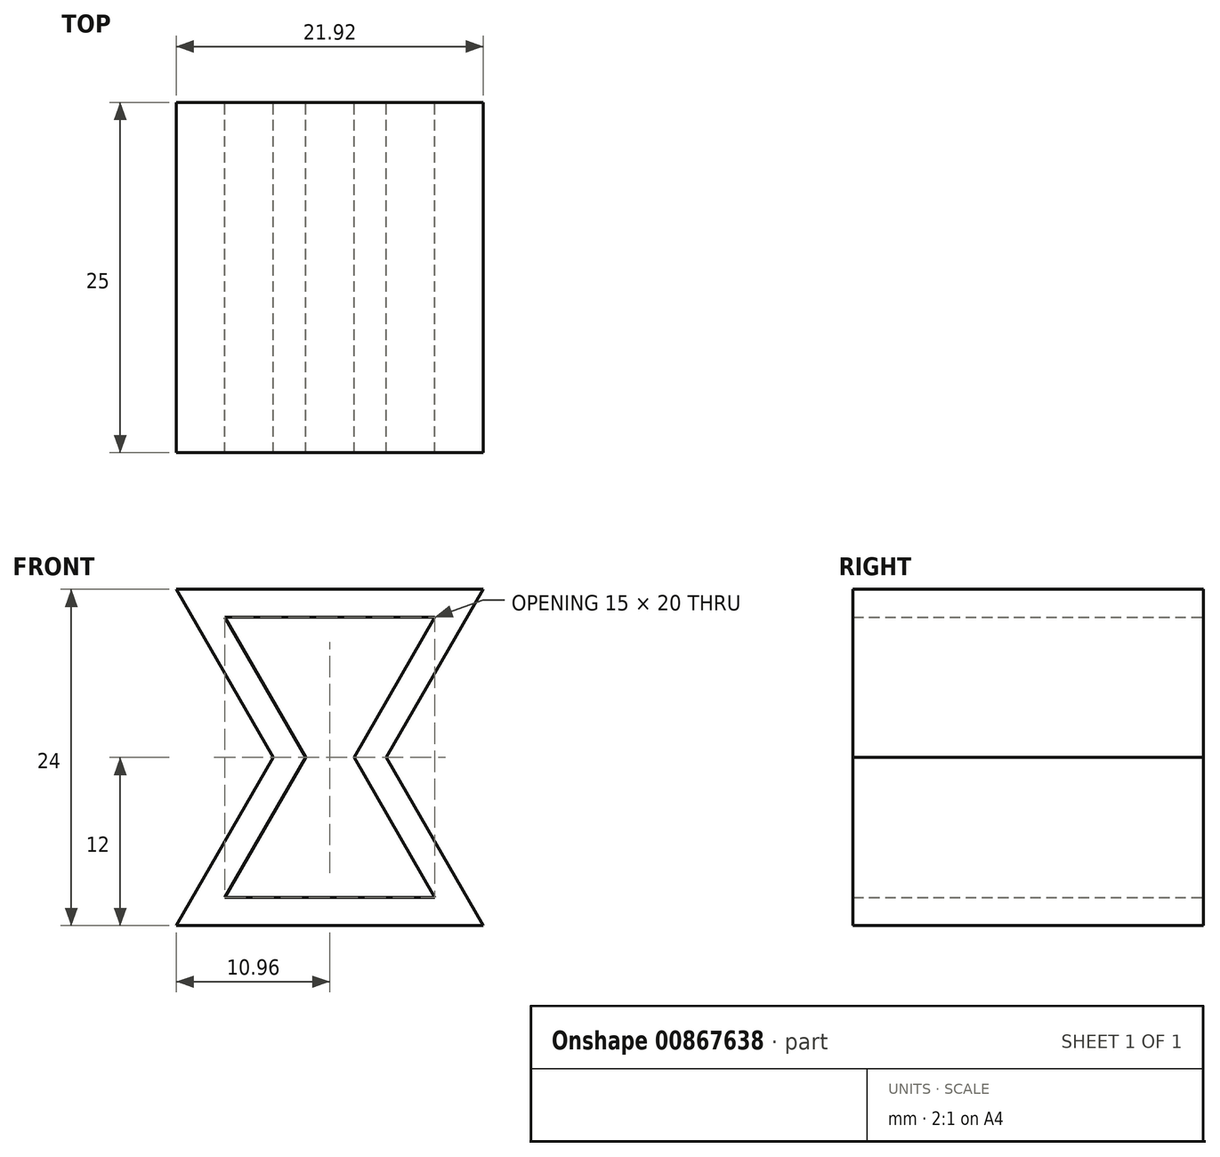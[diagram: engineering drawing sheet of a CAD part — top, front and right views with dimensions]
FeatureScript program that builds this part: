
annotation { "Feature Type Name" : "Feature", "Feature Type Description" : "" }
export const myFeature = defineFeature(function(context is Context, id is Id, definition is map)
    precondition{}
    {
        {
            var Q0;
            Q0=qCreatedBy(makeId("Front.planeOp"),FACE);
            var sketch = newSketch(context, id + "F0", { "sketchPlane" : qUnion([Q0])});
            skLineSegment(sketch, "E0", {"start": v(0, 0) * mm, "end": v(15, 0) * mm});
            skLineSegment(sketch, "E1", {"start": v(0, 20) * mm, "end": v(15, 20) * mm});
            skLineSegment(sketch, "E2", {"start": v(0, 20) * mm, "end": v(5.77, 10) * mm});
            skLineSegment(sketch, "E3", {"start": v(5.77, 10) * mm, "end": v(0, 0) * mm});
            skLineSegment(sketch, "E4", {"start": v(15, 20) * mm, "end": v(9.23, 10) * mm});
            skLineSegment(sketch, "E5", {"start": v(9.23, 10) * mm, "end": v(15, 0) * mm});
            skPoint(sketch, "E6", {"position": v(7.5, 22) * mm});
            skPoint(sketch, "E6.positionSnap0", {"position": v(7.5, 20) * mm});
            skPoint(sketch, "E7", {"position": v(7.5, -2) * mm});
            skPoint(sketch, "E7.positionSnap0", {"position": v(7.5, 0) * mm});
            skPoint(sketch, "E8", {"position": v(0.57, 5) * mm});
            skLineSegment(sketch, "E9", {"start": v(0.57, 5) * mm, "end": v(-3.46, -2) * mm});
            skPoint(sketch, "E10", {"position": v(14.43, 5) * mm});
            skLineSegment(sketch, "E11", {"start": v(14.43, 5) * mm, "end": v(18.46, -2) * mm});
            skPoint(sketch, "E12", {"position": v(14.52, 15.17) * mm});
            skPoint(sketch, "E13", {"position": v(-0.2, 16.35) * mm});
            skLineSegment(sketch, "E14", {"start": v(-0.2, 16.35) * mm, "end": v(-3.46, 22) * mm});
            skLineSegment(sketch, "E15", {"start": v(14.52, 15.17) * mm, "end": v(18.46, 22) * mm});
            skLineSegment(sketch, "E16", {"start": v(-3.46, 22) * mm, "end": v(18.46, 22) * mm});
            skLineSegment(sketch, "E17", {"start": v(-3.46, -2) * mm, "end": v(18.46, -2) * mm});
            skLineSegment(sketch, "E18", {"start": v(14.43, 5) * mm, "end": v(10.9, 11.1) * mm});
            skLineSegment(sketch, "E19", {"start": v(14.52, 15.17) * mm, "end": v(11.54, 10) * mm});
            skLineSegment(sketch, "E20", {"start": v(-0.2, 16.35) * mm, "end": v(3.46, 10) * mm});
            skLineSegment(sketch, "E21", {"start": v(3.46, 10) * mm, "end": v(0.57, 5) * mm});
            skSolve(sketch);
        }
        {
            var Q0;
            Q0=qSketchRegion(id+"F0",true);
            extrude(context, id + "F1", {"entities" : qUnion([Q0]), "depth" : 25 * mm, "offsetDistance" : 25 * mm});
        }
    });
